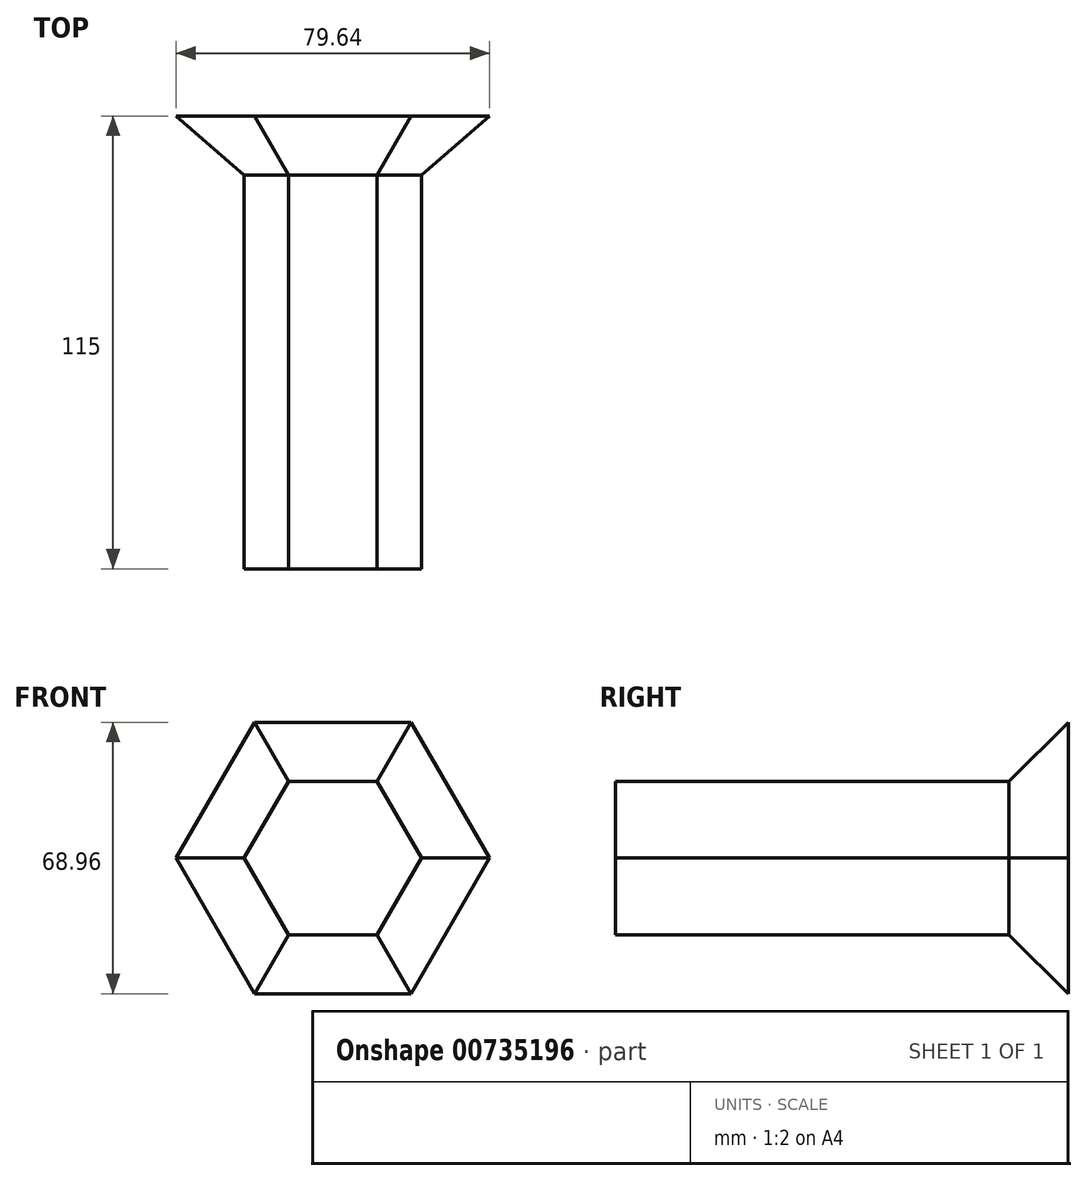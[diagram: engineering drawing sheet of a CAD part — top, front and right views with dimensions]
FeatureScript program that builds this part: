
annotation { "Feature Type Name" : "Feature", "Feature Type Description" : "" }
export const myFeature = defineFeature(function(context is Context, id is Id, definition is map)
    precondition{}
    {
        {
            var Q0;
            Q0=qCreatedBy(makeId("Front.planeOp"),FACE);
            var sketch = newSketch(context, id + "F0", { "sketchPlane" : qUnion([Q0])});
            skLineSegment(sketch, "E0.0", {"start": v(11.25, -19.48) * mm, "end": v(-11.25, -19.48) * mm});
            skLineSegment(sketch, "E0.1", {"start": v(-11.25, -19.48) * mm, "end": v(-22.5, 0) * mm});
            skLineSegment(sketch, "E0.2", {"start": v(-22.5, 0) * mm, "end": v(-11.25, 19.48) * mm});
            skLineSegment(sketch, "E0.3", {"start": v(-11.25, 19.48) * mm, "end": v(11.25, 19.48) * mm});
            skLineSegment(sketch, "E0.4", {"start": v(11.25, 19.48) * mm, "end": v(22.5, 0) * mm});
            skLineSegment(sketch, "E0.5", {"start": v(22.5, 0) * mm, "end": v(11.25, -19.48) * mm});
            skSolve(sketch);
        }
        {
            var Q0;
            Q0=makeQuery(id+"F0.imprint","IMPRINT",FACE,{"disambiguationData":[TD([[makeQuery(id+"F0.imprint","IMPRINT",EDGE,{"derivedFrom":sQuery(id+"F0.wireOp",EDGE,"E0.0")}),-1.0]])]});
            extrude(context, id + "F1", {"entities" : qUnion([Q0]), "depth" : 100 * mm, "offsetDistance" : 25 * mm});
        }
        {
            var Q0;
            Q0=makeQuery(id+"F1.opExtrude","CAP_FACE",FACE,{"disambiguationData":[OSD([sQuery(id+"F0.wireOp",EDGE,"E0.0"),sQuery(id+"F0.wireOp",EDGE,"E0.1"),sQuery(id+"F0.wireOp",EDGE,"E0.2"),sQuery(id+"F0.wireOp",EDGE,"E0.3"),sQuery(id+"F0.wireOp",EDGE,"E0.4"),sQuery(id+"F0.wireOp",EDGE,"E0.5")])],"isStart":true});
            extrude(context, id + "F2", {"entities" : qUnion([Q0]), "operationType" : NewBodyOperationType.ADD, "depth" : 15 * mm, "offsetDistance" : 25 * mm, "hasDraft" : true, "draftAngle" : 45 * degree});
        }
    });
